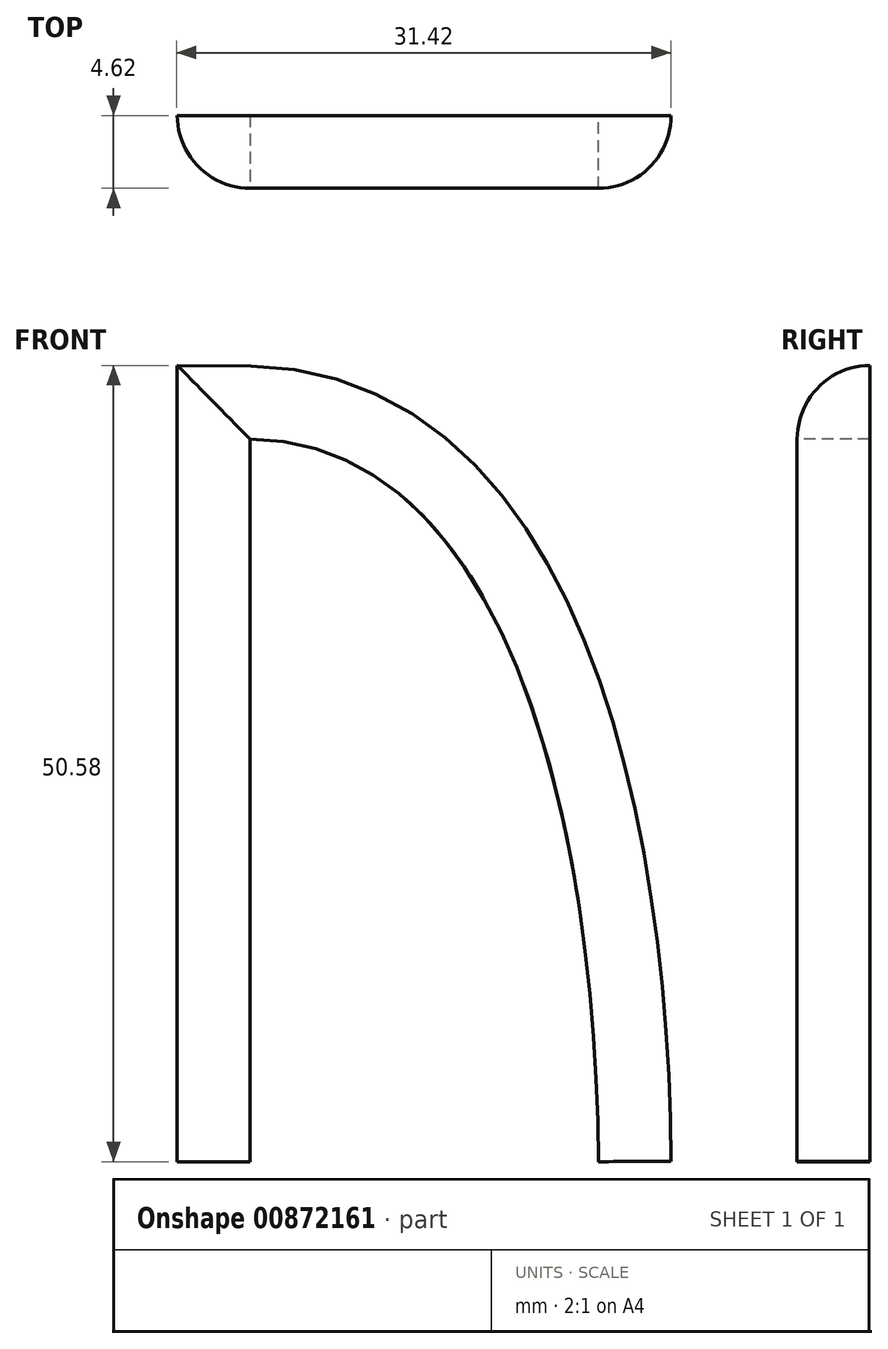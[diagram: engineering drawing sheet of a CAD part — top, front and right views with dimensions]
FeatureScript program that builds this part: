
annotation { "Feature Type Name" : "Feature", "Feature Type Description" : "" }
export const myFeature = defineFeature(function(context is Context, id is Id, definition is map)
    precondition{}
    {
        {
            var Q0;
            Q0=qCreatedBy(makeId("Front.planeOp"),FACE);
            var sketch = newSketch(context, id + "F0", { "sketchPlane" : qUnion([Q0])});
            skLineSegment(sketch, "E0", {"start": v(0, 0) * mm, "end": v(0, 45.9) * mm});
            skFitSpline(sketch, "E1", {"points": [v(0, 45.9) * mm, v(22.14, 0) * mm], "startDerivative": vector(51, -0.62) * mm, "endDerivative": vector(0.33, -58.85) * mm});
            skSolve(sketch);
        }
        {
            var Q0;
            Q0=qCreatedBy(makeId("Top.planeOp"),FACE);
            var sketch = newSketch(context, id + "F1", { "sketchPlane" : qUnion([Q0])});
            skArc(sketch, "E2", {"start": v(-4.62, 0) * mm, "mid": v(-3.27, -3.27) * mm, "end": v(0, -4.62) * mm});
            skLineSegment(sketch, "E3", {"start": v(-4.62, 0) * mm, "end": v(0, 0) * mm});
            skLineSegment(sketch, "E4", {"start": v(0, -4.62) * mm, "end": v(0, 0) * mm});
            skSolve(sketch);
        }
        {
            var Q0;
            Q0=makeQuery(id+"F1.imprint","IMPRINT",FACE,{"disambiguationData":[TD([[makeQuery(id+"F1.imprint","IMPRINT",EDGE,{"derivedFrom":sQuery(id+"F1.wireOp",EDGE,"E2")}),1.0]])]});
            var Q1;
            Q1=sQuery(id+"F0.wireOp",EDGE,"E0");
            var Q2;
            Q2=sQuery(id+"F0.wireOp",EDGE,"E1");
            sweep(context, id + "F2", {"profiles" : qUnion([Q0]), "path" : qUnion([Q1, Q2])});
        }
    });
